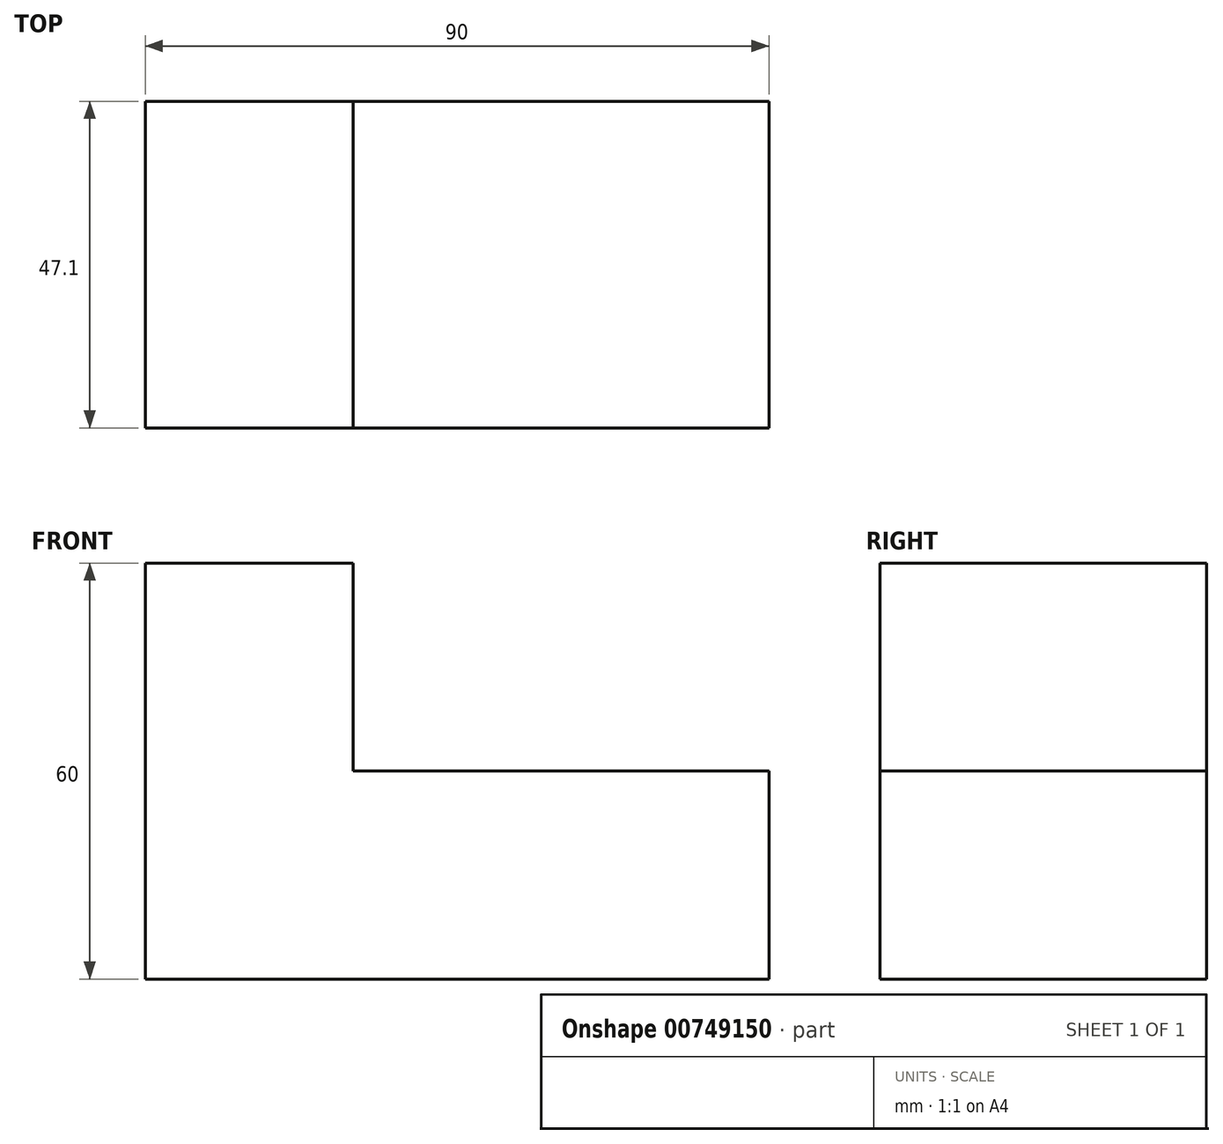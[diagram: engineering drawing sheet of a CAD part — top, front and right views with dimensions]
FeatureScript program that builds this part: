
annotation { "Feature Type Name" : "Feature", "Feature Type Description" : "" }
export const myFeature = defineFeature(function(context is Context, id is Id, definition is map)
    precondition{}
    {
        {
            var Q0;
            Q0=qCreatedBy(makeId("Front.planeOp"),FACE);
            var sketch = newSketch(context, id + "F0", { "sketchPlane" : qUnion([Q0])});
            skLineSegment(sketch, "E0", {"start": v(0, 0) * mm, "end": v(0, 30) * mm});
            skLineSegment(sketch, "E1", {"start": v(0, 30) * mm, "end": v(-60, 30) * mm});
            skLineSegment(sketch, "E2", {"start": v(-60, 30) * mm, "end": v(-60, 60) * mm});
            skLineSegment(sketch, "E3", {"start": v(-60, 60) * mm, "end": v(-90, 60) * mm});
            skLineSegment(sketch, "E4", {"start": v(-90, 60) * mm, "end": v(-90, 0) * mm});
            skLineSegment(sketch, "E5", {"start": v(-90, 0) * mm, "end": v(0, 0) * mm});
            skSolve(sketch);
        }
        {
            var Q0;
            Q0=makeQuery(id+"F0.imprint","IMPRINT",FACE,{"disambiguationData":[TD([[makeQuery(id+"F0.imprint","IMPRINT",EDGE,{"derivedFrom":sQuery(id+"F0.wireOp",EDGE,"E0")}),1.0]])]});
            extrude(context, id + "F1", {"entities" : qUnion([Q0]), "depth" : 47.1 * mm, "offsetDistance" : 25 * mm});
        }
    });
